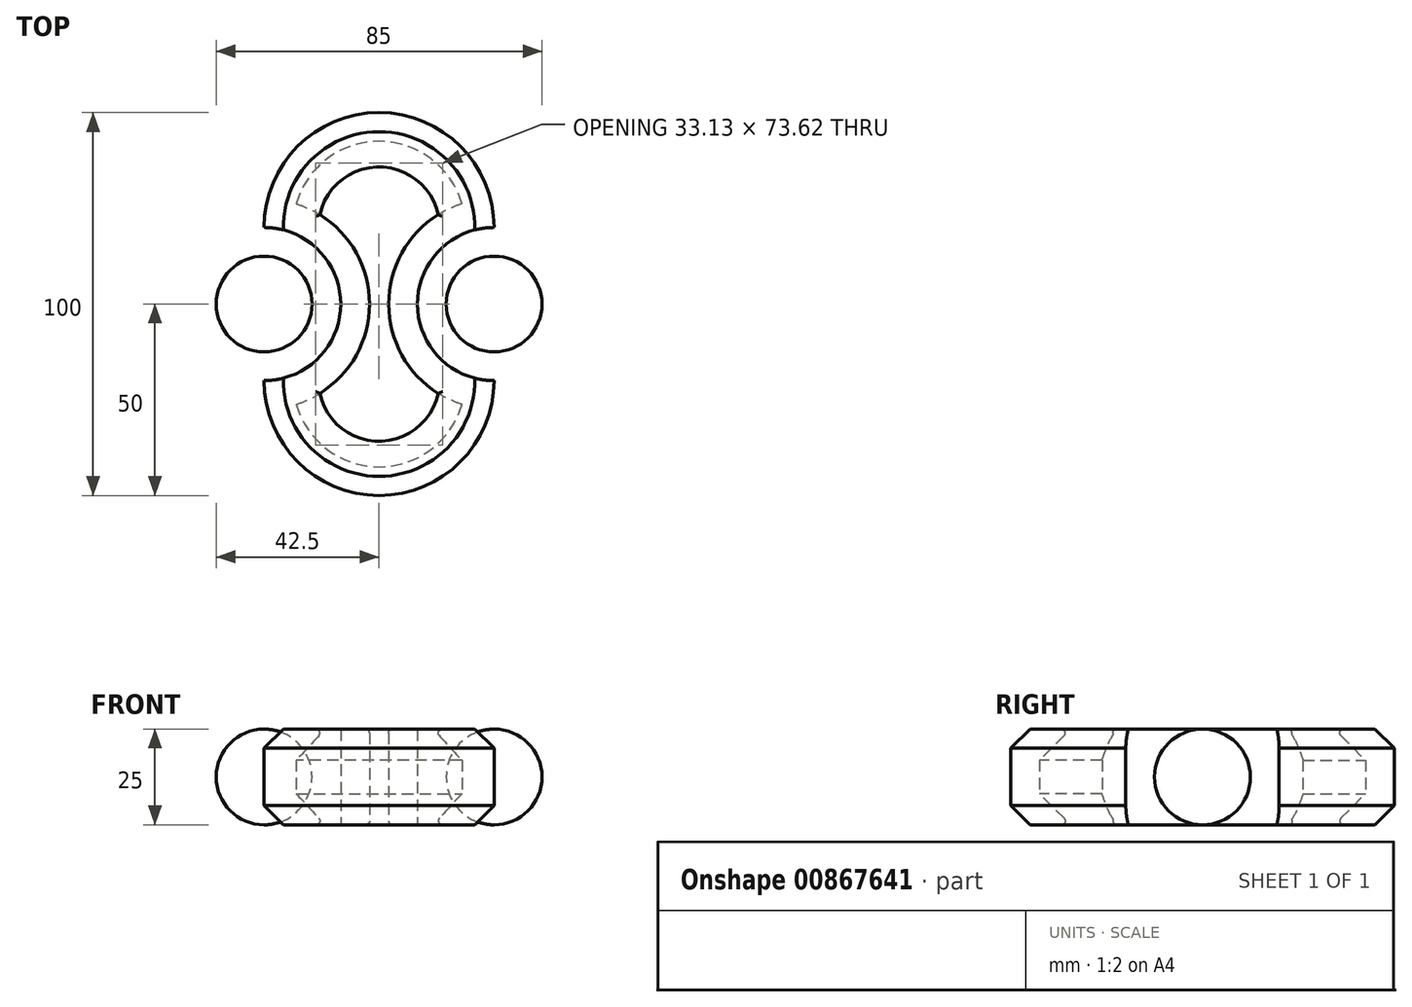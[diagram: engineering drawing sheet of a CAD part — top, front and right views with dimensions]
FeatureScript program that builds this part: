
annotation { "Feature Type Name" : "Feature", "Feature Type Description" : "" }
export const myFeature = defineFeature(function(context is Context, id is Id, definition is map)
    precondition{}
    {
        {
            var Q0;
            Q0=qCreatedBy(makeId("Top.planeOp"),FACE);
            var sketch = newSketch(context, id + "F0", { "sketchPlane" : qUnion([Q0])});
            skPoint(sketch, "E0.middle", {"position": v(0, 0) * mm});
            skArc(sketch, "E1", {"start": v(30, 20) * mm, "mid": v(10, 0) * mm, "end": v(30, -20) * mm});
            skArc(sketch, "E2", {"start": v(-30, -20) * mm, "mid": v(-10, 0) * mm, "end": v(-30, 20) * mm});
            skArc(sketch, "E3", {"start": v(-30, -20) * mm, "mid": v(0, -50) * mm, "end": v(30, -20) * mm});
            skArc(sketch, "E4.trimOffspring", {"start": v(30, 20) * mm, "mid": v(0, 50) * mm, "end": v(-30, 20) * mm});
            skCircle(sketch, "E5", {"center": v(-30, 0) * mm, "radius": 12.5 * mm});
            skCircle(sketch, "E6", {"center": v(30, 0) * mm, "radius": 12.5 * mm});
            skSolve(sketch);
        }
        {
            var Q0;
            Q0=makeQuery(id+"F0.imprint","IMPRINT",FACE,{"disambiguationData":[TD([[makeQuery(id+"F0.imprint","IMPRINT",EDGE,{"derivedFrom":sQuery(id+"F0.wireOp",EDGE,"E5")}),1.0]])]});
            var Q1;
            Q1=makeQuery(id+"F0.imprint","IMPRINT",FACE,{"disambiguationData":[TD([[makeQuery(id+"F0.imprint","IMPRINT",EDGE,{"derivedFrom":sQuery(id+"F0.wireOp",EDGE,"E1")}),-1.0]])]});
            var Q2;
            Q2=makeQuery(id+"F0.imprint","IMPRINT",FACE,{"disambiguationData":[TD([[makeQuery(id+"F0.imprint","IMPRINT",EDGE,{"derivedFrom":sQuery(id+"F0.wireOp",EDGE,"E6")}),1.0]])]});
            extrude(context, id + "F1", {"entities" : qUnion([Q0, Q1, Q2]), "depth" : 25 * mm, "offsetDistance" : 25 * mm});
        }
        {
            var Q0;
            Q0=makeQuery(id+"F1.opExtrude","CAP_EDGE",EDGE,{"disambiguationData":[OSD([sQuery(id+"F0.wireOp",EDGE,"E6")])],"isStart":false});
            var Q1;
            Q1=makeQuery(id+"F1.opExtrude","CAP_EDGE",EDGE,{"disambiguationData":[OSD([sQuery(id+"F0.wireOp",EDGE,"E6")])],"isStart":true});
            var Q2;
            Q2=makeQuery(id+"F1.opExtrude","CAP_EDGE",EDGE,{"disambiguationData":[OSD([sQuery(id+"F0.wireOp",EDGE,"E5")])],"isStart":false});
            var Q3;
            Q3=makeQuery(id+"F1.opExtrude","CAP_EDGE",EDGE,{"disambiguationData":[OSD([sQuery(id+"F0.wireOp",EDGE,"E5")])],"isStart":true});
            fillet(context, id + "F2", {"entities" : qUnion([Q0, Q1, Q2, Q3]), "radius" : 12.5 * mm, "tangentPropagation" : true, "allowEdgeOverflow" : false});
        }
        {
            var Q0;
            Q0=makeQuery(id+"F1.opExtrude","CAP_EDGE",EDGE,{"disambiguationData":[OSD([sQuery(id+"F0.wireOp",EDGE,"E3")])],"isStart":false});
            var Q1;
            Q1=makeQuery(id+"F1.opExtrude","CAP_EDGE",EDGE,{"disambiguationData":[OSD([sQuery(id+"F0.wireOp",EDGE,"E4.trimOffspring")])],"isStart":false});
            var Q2;
            Q2=makeQuery(id+"F1.opExtrude","CAP_EDGE",EDGE,{"disambiguationData":[OSD([sQuery(id+"F0.wireOp",EDGE,"E3")])],"isStart":true});
            var Q3;
            Q3=makeQuery(id+"F1.opExtrude","CAP_EDGE",EDGE,{"disambiguationData":[OSD([sQuery(id+"F0.wireOp",EDGE,"E4.trimOffspring")])],"isStart":true});
            chamfer(context, id + "F3", {"entities" : qUnion([Q0, Q1, Q2, Q3]), "width" : 5 * mm, "tangentPropagation" : true});
        }
        {
            var Q0;
            Q0=makeQuery(id+"F1.opExtrude","CAP_FACE",FACE,{"disambiguationData":[OSD([sQuery(id+"F0.wireOp",EDGE,"E1"),sQuery(id+"F0.wireOp",EDGE,"E2"),sQuery(id+"F0.wireOp",EDGE,"E3"),sQuery(id+"F0.wireOp",EDGE,"E4.trimOffspring")])],"isStart":false});
            var Q1;
            Q1=makeQuery(id+"F1.opExtrude","CAP_FACE",FACE,{"disambiguationData":[OSD([sQuery(id+"F0.wireOp",EDGE,"E1"),sQuery(id+"F0.wireOp",EDGE,"E2"),sQuery(id+"F0.wireOp",EDGE,"E3"),sQuery(id+"F0.wireOp",EDGE,"E4.trimOffspring")])],"isStart":true});
            shell(context, id + "F4", {"entities" : qUnion([Q0, Q1]), "thickness" : 7.5 * mm});
        }
        {
            var Q0;
            {var subQ0=sQuery(id+"F0.wireOp",EDGE,"E1");Q0=makeQuery(id+"F4.opShell","OFFSET_EDGE",EDGE,{"disambiguationData":[OSD([subQ0]),TDD([makeQuery(id+"F1.opExtrude","CAP_EDGE",EDGE,{"disambiguationData":[OSD([subQ0])],"isStart":false})])]});}
            var Q1;
            {var subQ0=sQuery(id+"F0.wireOp",EDGE,"E2");Q1=makeQuery(id+"F4.opShell","OFFSET_EDGE",EDGE,{"disambiguationData":[OSD([subQ0]),TDD([makeQuery(id+"F1.opExtrude","CAP_EDGE",EDGE,{"disambiguationData":[OSD([subQ0])],"isStart":false})])]});}
            var Q2;
            {var subQ0=sQuery(id+"F0.wireOp",EDGE,"E4.trimOffspring");var subQ1=sQuery(id+"F0.wireOp",EDGE,"E3");var subQ2=sQuery(id+"F0.wireOp",EDGE,"E2");var subQ3=sQuery(id+"F0.wireOp",EDGE,"E1");Q2=makeQuery(id+"F4.opShell","OFFSET_EDGE",EDGE,{"disambiguationData":[OSD([subQ3,subQ2,subQ1,subQ0]),TDD([makeQuery(id+"F3.opChamfer","BLEND_EDGE",EDGE,{"blendedFrom":[makeQuery(id+"F1.opExtrude","CAP_EDGE",EDGE,{"disambiguationData":[OSD([subQ0])],"isStart":false}),makeQuery(id+"F1.opExtrude","CAP_FACE",FACE,{"disambiguationData":[OSD([subQ3,subQ2,subQ1,subQ0])],"isStart":false})],"blendedInto":[makeQuery(id+"F1.opExtrude","CAP_FACE",FACE,{"disambiguationData":[OSD([subQ3,subQ2,subQ1,subQ0])],"isStart":false})]})])]});}
            var Q3;
            {var subQ0=sQuery(id+"F0.wireOp",EDGE,"E4.trimOffspring");var subQ1=sQuery(id+"F0.wireOp",EDGE,"E3");var subQ2=sQuery(id+"F0.wireOp",EDGE,"E2");var subQ3=sQuery(id+"F0.wireOp",EDGE,"E1");Q3=makeQuery(id+"F4.opShell","OFFSET_EDGE",EDGE,{"disambiguationData":[OSD([subQ3,subQ2,subQ1,subQ0]),TDD([makeQuery(id+"F3.opChamfer","BLEND_EDGE",EDGE,{"blendedFrom":[makeQuery(id+"F1.opExtrude","CAP_EDGE",EDGE,{"disambiguationData":[OSD([subQ1])],"isStart":false}),makeQuery(id+"F1.opExtrude","CAP_FACE",FACE,{"disambiguationData":[OSD([subQ3,subQ2,subQ1,subQ0])],"isStart":false})],"blendedInto":[makeQuery(id+"F1.opExtrude","CAP_FACE",FACE,{"disambiguationData":[OSD([subQ3,subQ2,subQ1,subQ0])],"isStart":false})]})])]});}
            var Q4;
            {var subQ0=sQuery(id+"F0.wireOp",EDGE,"E2");Q4=makeQuery(id+"F4.opShell","OFFSET_EDGE",EDGE,{"disambiguationData":[OSD([subQ0]),TDD([makeQuery(id+"F1.opExtrude","CAP_EDGE",EDGE,{"disambiguationData":[OSD([subQ0])],"isStart":true})])]});}
            var Q5;
            {var subQ0=sQuery(id+"F0.wireOp",EDGE,"E1");Q5=makeQuery(id+"F4.opShell","OFFSET_EDGE",EDGE,{"disambiguationData":[OSD([subQ0]),TDD([makeQuery(id+"F1.opExtrude","CAP_EDGE",EDGE,{"disambiguationData":[OSD([subQ0])],"isStart":true})])]});}
            var Q6;
            {var subQ0=sQuery(id+"F0.wireOp",EDGE,"E4.trimOffspring");var subQ1=sQuery(id+"F0.wireOp",EDGE,"E3");var subQ2=sQuery(id+"F0.wireOp",EDGE,"E2");var subQ3=sQuery(id+"F0.wireOp",EDGE,"E1");Q6=makeQuery(id+"F4.opShell","OFFSET_EDGE",EDGE,{"disambiguationData":[OSD([subQ3,subQ2,subQ1,subQ0]),TDD([makeQuery(id+"F3.opChamfer","BLEND_EDGE",EDGE,{"blendedFrom":[makeQuery(id+"F1.opExtrude","CAP_EDGE",EDGE,{"disambiguationData":[OSD([subQ1])],"isStart":true}),makeQuery(id+"F1.opExtrude","CAP_FACE",FACE,{"disambiguationData":[OSD([subQ3,subQ2,subQ1,subQ0])],"isStart":true})],"blendedInto":[makeQuery(id+"F1.opExtrude","CAP_FACE",FACE,{"disambiguationData":[OSD([subQ3,subQ2,subQ1,subQ0])],"isStart":true})]})])]});}
            var Q7;
            {var subQ0=sQuery(id+"F0.wireOp",EDGE,"E4.trimOffspring");var subQ1=sQuery(id+"F0.wireOp",EDGE,"E3");var subQ2=sQuery(id+"F0.wireOp",EDGE,"E2");var subQ3=sQuery(id+"F0.wireOp",EDGE,"E1");Q7=makeQuery(id+"F4.opShell","OFFSET_EDGE",EDGE,{"disambiguationData":[OSD([subQ3,subQ2,subQ1,subQ0]),TDD([makeQuery(id+"F3.opChamfer","BLEND_EDGE",EDGE,{"blendedFrom":[makeQuery(id+"F1.opExtrude","CAP_EDGE",EDGE,{"disambiguationData":[OSD([subQ0])],"isStart":true}),makeQuery(id+"F1.opExtrude","CAP_FACE",FACE,{"disambiguationData":[OSD([subQ3,subQ2,subQ1,subQ0])],"isStart":true})],"blendedInto":[makeQuery(id+"F1.opExtrude","CAP_FACE",FACE,{"disambiguationData":[OSD([subQ3,subQ2,subQ1,subQ0])],"isStart":true})]})])]});}
            fillet(context, id + "F5", {"entities" : qUnion([Q0, Q1, Q2, Q3, Q4, Q5, Q6, Q7]), "radius" : 1 * mm, "tangentPropagation" : true, "allowEdgeOverflow" : false});
        }
    });
